# Revit family: Safety & Protection_Barrier_UltiGroup_Pedestrian Swing Gate
name_source: partatom
category: Generic Models
revit_build: Autodesk Revit Architecture 2016 (Build: 20150220_1215(x64)
units: mm (PartAtom-declared; Revit-internal decimal feet)

## family parameters
Always vertical = Yes
Can host rebar = No
Cut with Voids When Loaded = No
OmniClass Number = 23.40.70.17
OmniClass Title = Industrial and Manufacturing Equipment and Furnishings
Part Type = Normal
Room Calculation Point = No
Round Connector Dimension = Use Diameter
Shared = No
Work Plane-Based = No

## types (1)
- Type 1
    Bollard Post = Yes
    Description = Impactable PVC Pedestrian Swing Gate
    Fax = 07 846 2467
    Hinge Parts = Hinge Parts
    InstallationGroup_ANZRS = 0
    Manufacturer = UltiGroup
    Model = Ulti Pedestrian Swing Gate - DP150
    ModifiedIssue_ANZRS = 0 $
    PVC Yellow = PVC Yellow
    Pedestrian Gate width = 850 mm  [stored 2.78871 ft]
    Send Message = http://ultigroup.co.nz
    Stainless Steel = SS Bolts
    URL = www.ultigroup.co.nz

note: [stored X ft] marks values corroborated as IEEE doubles in the binary element streams (Revit-internal decimal feet)

## geometry (parser evidence)
native form markers: Blend x2, Sweep x4
no freeform markers — native parametric forms only
